# Revit family: lgh-n15_35rkx2(d)_rks2(d)_60Hz
name_source: partatom
category: 機械設備
units: mm (PartAtom-declared; Revit-internal decimal feet)

## family parameters
OmniClass タイトル = Heat Exchangers for Ventilation Air
OmniClass 番号 = 23.75.10.34.21
パーツ タイプ = 標準
ロード時にボイドで切り取り = いいえ
丸型コネクタ寸法 = 直径を使用
作業面ベース = いいえ
共有 = いいえ
常に垂直 = はい
部屋計算ポイント = はい

## types (12) — shared parameters
Box_Depth = 172  [stored 0.564304 ft]
Box_Height = 262  [stored 0.85958 ft]
Box_Width = 115  [stored 0.377297 ft]
Clearance Left = 600
EAダクト接続口方向_変更 = いいえ
EAダクト接続口方向_標準 = はい
IfcExportAs = IfcAirToAirHeatRecoveryType
IfcExportType = ROTARYWHEEL
OAダクト接続口方向_変更 = いいえ
OAダクト接続口方向_標準 = はい
OmniClassCode = 23-27 23 19 11
URL = https://www.mitsubishielectric.co.jp
Uniclass2015Code = Pr_60_60_36_88
Uniclass2015Title = Thermal wheels
Uniclass2015Version = Systems v1.9
ドレン管_D = 307  [stored 1.00722 ft]
ドレン管_Depth = 10  [stored 0.0328084 ft]
ドレン管_H = 25  [stored 0.082021 ft]
ドレン管径 = 32 mm
メンテナンススペース = はい
仕様書バージョン = Version1.0
企業コード = 108420
分類コード = 50052504100070
初期抵抗 = 0.0 Pa
加湿給水管径 = 22 mm
周波数 = 60 Hz
呼称 = 全熱交換ユニット
外気量 = 0.0 m³/h
天吊金具_幅 = 20  [stored 0.0656168 ft]
天吊金具_径 = 7  [stored 0.0229659 ft]
実風量 = 0.0 m³/h
形式 = 天井埋込ダクト形
排気量 = 0.0 m³/h
本体マテリアル = 溶融亜鉛めっき鋼板
法定耐用年数 = 15
消費電力_加湿器 = 0 W
点検口 = はい
点検口1_Depth = 450  [stored 1.47638 ft]
点検口1_Width = 450  [stored 1.47638 ft]
点検口離隔 = 150
相 = 1
積算_科目 = 1 空気調和設備
符号 = HEU
給水管_D = 358  [stored 1.17454 ft]
給水管_Depth = 10  [stored 0.0328084 ft]
給水管_H = 92  [stored 0.301837 ft]
製品リリース年月 = 2015/1/30
製品出荷対象 = 国内
製造元 = 三菱電機株式会社
設置方法 = 天井吊(隠ぺい)形
設計風量 = 0.0 m³/h
説明 = 業務用ロスナイ 天井埋込形加湿付
負荷分類 = 3_ファン類
運転質量 = 0.00 kg
電動機出力 = 0 W
zero-valued in all types: Clearance Bottom, Clearance Top, EAサイズ_W, OAサイズ_W, RAサイズ_W, SAサイズ_W

## per-type parameters (varying)
- LGH-N15RKS2: Box_D=446  [stored 1.46325 ft]; Box_H=20  [stored 0.0656168 ft]; Depth=1182; Duct_Change_Center=119  [stored 0.39042 ft]; Duct_Depth=53  [stored 0.173885 ft]; Duct_Height=95; Duct_Height_SA=149  [stored 0.488845 ft]; Duct_Pitch_OA_EA=450  [stored 1.47638 ft]; Duct_Pitch_SA_RA=400  [stored 1.31234 ft]; Duct_Width_RA=225  [stored 0.738189 ft]; EAサイズ_D=98; Height=298  [stored 0.97769 ft]; MAX静圧=130.0 Pa; MAX風量=150.0 m³/h; MID静圧=60.0 Pa; MID風量=100.0 m³/h; MIN静圧=15.0 Pa; MIN風量=50.0 m³/h; OAサイズ_D=98; RAサイズ_D=98; SAサイズ_D=98; SMAX静圧=0.0 Pa; SMAX風量=0.0 m³/h; Width=611; エンタルピ交換効率_冷房=68.00%; エンタルピ交換効率_暖房=69.00%; 価格=328000 $; 吊りボルト_高さ=75; 吊りボルトピッチ1=658; 吊りボルトピッチ2=1169; 有効加湿量=0.44; 極数=2; 機外静圧=130.0 Pa; 機外静圧_排気=130.0 Pa; 消費電力=133 W; 温度交換効率=74.00%; 点検口1_Center=656; 点検口高さ=-298  [stored -0.97769 ft]; 製品質量=33.00 kg; 質量=39.60 kg; 電圧=100 V; 面風速=5.3 m/s; 風量=150.0 m³/h; 騒音レベル(dB(A))=29
- LGH-N15RKS2D: Box_D=446  [stored 1.46325 ft]; Box_H=20  [stored 0.0656168 ft]; Depth=1182; Duct_Change_Center=119  [stored 0.39042 ft]; Duct_Depth=53  [stored 0.173885 ft]; Duct_Height=95; Duct_Height_SA=149  [stored 0.488845 ft]; Duct_Pitch_OA_EA=450  [stored 1.47638 ft]; Duct_Pitch_SA_RA=400  [stored 1.31234 ft]; Duct_Width_RA=225  [stored 0.738189 ft]; EAサイズ_D=98; Height=298  [stored 0.97769 ft]; MAX静圧=130.0 Pa; MAX風量=150.0 m³/h; MID静圧=60.0 Pa; MID風量=100.0 m³/h; MIN静圧=21.0 Pa; MIN風量=60.0 m³/h; OAサイズ_D=98; RAサイズ_D=98; SAサイズ_D=98; SMAX静圧=0.0 Pa; SMAX風量=0.0 m³/h; Width=611; エンタルピ交換効率_冷房=68.00%; エンタルピ交換効率_暖房=69.00%; 価格=328000 $; 吊りボルト_高さ=75; 吊りボルトピッチ1=658; 吊りボルトピッチ2=1169; 有効加湿量=0.44; 極数=3; 機外静圧=130.0 Pa; 機外静圧_排気=130.0 Pa; 消費電力=125 W; 温度交換効率=74.00%; 点検口1_Center=656; 点検口高さ=-298  [stored -0.97769 ft]; 製品質量=33.00 kg; 質量=39.60 kg; 電圧=200 V; 面風速=5.3 m/s; 風量=150.0 m³/h; 騒音レベル(dB(A))=29
- LGH-N15RKX2: Box_D=446  [stored 1.46325 ft]; Box_H=20  [stored 0.0656168 ft]; Depth=1182; Duct_Change_Center=119  [stored 0.39042 ft]; Duct_Depth=53  [stored 0.173885 ft]; Duct_Height=95; Duct_Height_SA=149  [stored 0.488845 ft]; Duct_Pitch_OA_EA=450  [stored 1.47638 ft]; Duct_Pitch_SA_RA=400  [stored 1.31234 ft]; Duct_Width_RA=225  [stored 0.738189 ft]; EAサイズ_D=98; Height=298  [stored 0.97769 ft]; MAX静圧=130.0 Pa; MAX風量=150.0 m³/h; MID静圧=60.0 Pa; MID風量=100.0 m³/h; MIN静圧=15.0 Pa; MIN風量=50.0 m³/h; OAサイズ_D=98; RAサイズ_D=98; SAサイズ_D=98; SMAX静圧=0.0 Pa; SMAX風量=0.0 m³/h; Width=611; エンタルピ交換効率_冷房=68.00%; エンタルピ交換効率_暖房=69.00%; 価格=475000 $; 参照している仕様書等のバージョン=公共建築工事標準仕様書（機械設備工事編）平成31年度版; 吊りボルト_高さ=75; 吊りボルトピッチ1=658; 吊りボルトピッチ2=1169; 有効加湿量=0.44; 極数=2; 機外静圧=130.0 Pa; 機外静圧_排気=130.0 Pa; 消費電力=133 W; 温度交換効率=74.00%; 点検口1_Center=656; 点検口高さ=-298  [stored -0.97769 ft]; 製品質量=33.00 kg; 質量=39.60 kg; 電圧=100 V; 面風速=5.3 m/s; 風量=150.0 m³/h; 騒音レベル(dB(A))=29
- LGH-N15RKX2D: Box_D=446  [stored 1.46325 ft]; Box_H=20  [stored 0.0656168 ft]; Depth=1182; Duct_Change_Center=119  [stored 0.39042 ft]; Duct_Depth=53  [stored 0.173885 ft]; Duct_Height=95; Duct_Height_SA=149  [stored 0.488845 ft]; Duct_Pitch_OA_EA=450  [stored 1.47638 ft]; Duct_Pitch_SA_RA=400  [stored 1.31234 ft]; Duct_Width_RA=225  [stored 0.738189 ft]; EAサイズ_D=98; Height=298  [stored 0.97769 ft]; MAX静圧=130.0 Pa; MAX風量=150.0 m³/h; MID静圧=60.0 Pa; MID風量=100.0 m³/h; MIN静圧=21.0 Pa; MIN風量=60.0 m³/h; OAサイズ_D=98; RAサイズ_D=98; SAサイズ_D=98; SMAX静圧=0.0 Pa; SMAX風量=0.0 m³/h; Width=611; エンタルピ交換効率_冷房=68.00%; エンタルピ交換効率_暖房=69.00%; 価格=475000 $; 参照している仕様書等のバージョン=公共建築工事標準仕様書（機械設備工事編）平成31年度版; 吊りボルト_高さ=75; 吊りボルトピッチ1=658; 吊りボルトピッチ2=1169; 有効加湿量=0.44; 極数=3; 機外静圧=130.0 Pa; 機外静圧_排気=130.0 Pa; 消費電力=125 W; 温度交換効率=74.00%; 点検口1_Center=656; 点検口高さ=-298  [stored -0.97769 ft]; 製品質量=33.00 kg; 質量=39.60 kg; 電圧=200 V; 面風速=5.3 m/s; 風量=150.0 m³/h; 騒音レベル(dB(A))=29
- LGH-N25RKS2: Box_D=476  [stored 1.56168 ft]; Box_H=20  [stored 0.0656168 ft]; Depth=1212; Duct_Change_Center=102; Duct_Depth=63  [stored 0.206693 ft]; Duct_Height=115  [stored 0.377297 ft]; Duct_Height_SA=149  [stored 0.488845 ft]; Duct_Pitch_OA_EA=530  [stored 1.73885 ft]; Duct_Pitch_SA_RA=505  [stored 1.65682 ft]; Duct_Width_RA=265  [stored 0.869423 ft]; EAサイズ_D=142  [stored 0.465879 ft]; Height=298  [stored 0.97769 ft]; MAX静圧=90.0 Pa; MAX風量=250.0 m³/h; MID静圧=30.0 Pa; MID風量=145.0 m³/h; MIN静圧=7.0 Pa; MIN風量=70.0 m³/h; OAサイズ_D=142  [stored 0.465879 ft]; RAサイズ_D=142  [stored 0.465879 ft]; SAサイズ_D=142  [stored 0.465879 ft]; SMAX静圧=0.0 Pa; SMAX風量=0.0 m³/h; Width=735; エンタルピ交換効率_冷房=68.00%; エンタルピ交換効率_暖房=69.00%; 価格=356000 $; 吊りボルト_高さ=75; 吊りボルトピッチ1=782; 吊りボルトピッチ2=1199; 有効加湿量=0.73; 極数=2; 機外静圧=90.0 Pa; 機外静圧_排気=90.0 Pa; 消費電力=162 W; 温度交換効率=74.00%; 点検口1_Center=656; 点検口高さ=-298  [stored -0.97769 ft]; 製品質量=36.00 kg; 質量=43.20 kg; 電圧=100 V; 面風速=3.9 m/s; 風量=250.0 m³/h; 騒音レベル(dB(A))=29
- LGH-N25RKS2D: Box_D=476  [stored 1.56168 ft]; Box_H=20  [stored 0.0656168 ft]; Depth=1212; Duct_Change_Center=102; Duct_Depth=63  [stored 0.206693 ft]; Duct_Height=115  [stored 0.377297 ft]; Duct_Height_SA=149  [stored 0.488845 ft]; Duct_Pitch_OA_EA=530  [stored 1.73885 ft]; Duct_Pitch_SA_RA=505  [stored 1.65682 ft]; Duct_Width_RA=265  [stored 0.869423 ft]; EAサイズ_D=142  [stored 0.465879 ft]; Height=298  [stored 0.97769 ft]; MAX静圧=90.0 Pa; MAX風量=250.0 m³/h; MID静圧=35.0 Pa; MID風量=155.0 m³/h; MIN静圧=7.0 Pa; MIN風量=70.0 m³/h; OAサイズ_D=142  [stored 0.465879 ft]; RAサイズ_D=142  [stored 0.465879 ft]; SAサイズ_D=142  [stored 0.465879 ft]; SMAX静圧=0.0 Pa; SMAX風量=0.0 m³/h; Width=735; エンタルピ交換効率_冷房=68.00%; エンタルピ交換効率_暖房=69.00%; 価格=356000 $; 吊りボルト_高さ=75; 吊りボルトピッチ1=782; 吊りボルトピッチ2=1199; 有効加湿量=0.73; 極数=3; 機外静圧=90.0 Pa; 機外静圧_排気=90.0 Pa; 消費電力=173 W; 温度交換効率=74.00%; 点検口1_Center=656; 点検口高さ=-298  [stored -0.97769 ft]; 製品質量=36.00 kg; 質量=43.20 kg; 電圧=200 V; 面風速=3.9 m/s; 風量=250.0 m³/h; 騒音レベル(dB(A))=29
- LGH-N25RKX2: Box_D=476  [stored 1.56168 ft]; Box_H=20  [stored 0.0656168 ft]; Depth=1212; Duct_Change_Center=102; Duct_Depth=63  [stored 0.206693 ft]; Duct_Height=115  [stored 0.377297 ft]; Duct_Height_SA=149  [stored 0.488845 ft]; Duct_Pitch_OA_EA=530  [stored 1.73885 ft]; Duct_Pitch_SA_RA=505  [stored 1.65682 ft]; Duct_Width_RA=265  [stored 0.869423 ft]; EAサイズ_D=142  [stored 0.465879 ft]; Height=298  [stored 0.97769 ft]; MAX静圧=90.0 Pa; MAX風量=250.0 m³/h; MID静圧=30.0 Pa; MID風量=145.0 m³/h; MIN静圧=7.0 Pa; MIN風量=70.0 m³/h; OAサイズ_D=142  [stored 0.465879 ft]; RAサイズ_D=142  [stored 0.465879 ft]; SAサイズ_D=142  [stored 0.465879 ft]; SMAX静圧=0.0 Pa; SMAX風量=0.0 m³/h; Width=735; エンタルピ交換効率_冷房=68.00%; エンタルピ交換効率_暖房=69.00%; 価格=515000 $; 参照している仕様書等のバージョン=公共建築工事標準仕様書（機械設備工事編）平成31年度版; 吊りボルト_高さ=75; 吊りボルトピッチ1=782; 吊りボルトピッチ2=1199; 有効加湿量=0.73; 極数=2; 機外静圧=90.0 Pa; 機外静圧_排気=90.0 Pa; 消費電力=162 W; 温度交換効率=74.00%; 点検口1_Center=656; 点検口高さ=-298  [stored -0.97769 ft]; 製品質量=36.00 kg; 質量=43.20 kg; 電圧=100 V; 面風速=3.9 m/s; 風量=250.0 m³/h; 騒音レベル(dB(A))=29
- LGH-N25RKX2D: Box_D=476  [stored 1.56168 ft]; Box_H=20  [stored 0.0656168 ft]; Depth=1212; Duct_Change_Center=102; Duct_Depth=63  [stored 0.206693 ft]; Duct_Height=115  [stored 0.377297 ft]; Duct_Height_SA=149  [stored 0.488845 ft]; Duct_Pitch_OA_EA=530  [stored 1.73885 ft]; Duct_Pitch_SA_RA=505  [stored 1.65682 ft]; Duct_Width_RA=265  [stored 0.869423 ft]; EAサイズ_D=142  [stored 0.465879 ft]; Height=298  [stored 0.97769 ft]; MAX静圧=90.0 Pa; MAX風量=250.0 m³/h; MID静圧=35.0 Pa; MID風量=155.0 m³/h; MIN静圧=7.0 Pa; MIN風量=70.0 m³/h; OAサイズ_D=142  [stored 0.465879 ft]; RAサイズ_D=142  [stored 0.465879 ft]; SAサイズ_D=142  [stored 0.465879 ft]; SMAX静圧=0.0 Pa; SMAX風量=0.0 m³/h; Width=735; エンタルピ交換効率_冷房=68.00%; エンタルピ交換効率_暖房=69.00%; 価格=515000 $; 参照している仕様書等のバージョン=公共建築工事標準仕様書（機械設備工事編）平成31年度版; 吊りボルト_高さ=75; 吊りボルトピッチ1=782; 吊りボルトピッチ2=1199; 有効加湿量=0.73; 極数=3; 機外静圧=90.0 Pa; 機外静圧_排気=90.0 Pa; 消費電力=173 W; 温度交換効率=74.00%; 点検口1_Center=656; 点検口高さ=-298  [stored -0.97769 ft]; 製品質量=36.00 kg; 質量=43.20 kg; 電圧=200 V; 面風速=3.9 m/s; 風量=250.0 m³/h; 騒音レベル(dB(A))=29
- LGH-N35RKS2: Box_D=476  [stored 1.56168 ft]; Box_H=12  [stored 0.0393701 ft]; Depth=1288; Duct_Change_Center=124  [stored 0.406824 ft]; Duct_Depth=64  [stored 0.209974 ft]; Duct_Height=110  [stored 0.360892 ft]; Duct_Height_SA=165; Duct_Pitch_OA_EA=650; Duct_Pitch_SA_RA=400  [stored 1.31234 ft]; Duct_Width_RA=325  [stored 1.06627 ft]; EAサイズ_D=142  [stored 0.465879 ft]; Height=331  [stored 1.08596 ft]; MAX静圧=85.0 Pa; MAX風量=350.0 m³/h; MID静圧=50.0 Pa; MID風量=250.0 m³/h; MIN静圧=7.0 Pa; MIN風量=110.0 m³/h; OAサイズ_D=142  [stored 0.465879 ft]; RAサイズ_D=142  [stored 0.465879 ft]; SAサイズ_D=142  [stored 0.465879 ft]; SMAX静圧=170.0 Pa; SMAX風量=350.0 m³/h; Width=874; エンタルピ交換効率_冷房=70.00%; エンタルピ交換効率_暖房=71.00%; 価格=406000 $; 吊りボルト_高さ=85  [stored 0.278871 ft]; 吊りボルトピッチ1=922; 吊りボルトピッチ2=1275; 有効加湿量=1.01; 極数=2; 機外静圧=170.0 Pa; 機外静圧_排気=170.0 Pa; 消費電力=227 W; 温度交換効率=75.00%; 点検口1_Center=732; 点検口高さ=-331  [stored -1.08596 ft]; 製品質量=44.00 kg; 質量=52.80 kg; 電圧=100 V; 面風速=5.5 m/s; 風量=350.0 m³/h; 騒音レベル(dB(A))=32.5
- LGH-N35RKS2D: Box_D=476  [stored 1.56168 ft]; Box_H=12  [stored 0.0393701 ft]; Depth=1288; Duct_Change_Center=124  [stored 0.406824 ft]; Duct_Depth=64  [stored 0.209974 ft]; Duct_Height=110  [stored 0.360892 ft]; Duct_Height_SA=165; Duct_Pitch_OA_EA=650; Duct_Pitch_SA_RA=400  [stored 1.31234 ft]; Duct_Width_RA=325  [stored 1.06627 ft]; EAサイズ_D=142  [stored 0.465879 ft]; Height=331  [stored 1.08596 ft]; MAX静圧=85.0 Pa; MAX風量=350.0 m³/h; MID静圧=40.0 Pa; MID風量=245.0 m³/h; MIN静圧=10.0 Pa; MIN風量=135.0 m³/h; OAサイズ_D=142  [stored 0.465879 ft]; RAサイズ_D=142  [stored 0.465879 ft]; SAサイズ_D=142  [stored 0.465879 ft]; SMAX静圧=170.0 Pa; SMAX風量=350.0 m³/h; Width=874; エンタルピ交換効率_冷房=70.00%; エンタルピ交換効率_暖房=71.00%; 価格=406000 $; 吊りボルト_高さ=85  [stored 0.278871 ft]; 吊りボルトピッチ1=922; 吊りボルトピッチ2=1275; 有効加湿量=1.01; 極数=3; 機外静圧=170.0 Pa; 機外静圧_排気=170.0 Pa; 消費電力=212 W; 温度交換効率=75.00%; 点検口1_Center=732; 点検口高さ=-331  [stored -1.08596 ft]; 製品質量=44.00 kg; 質量=52.80 kg; 電圧=200 V; 面風速=5.5 m/s; 風量=350.0 m³/h; 騒音レベル(dB(A))=32.5
- LGH-N35RKX2: Box_D=476  [stored 1.56168 ft]; Box_H=12  [stored 0.0393701 ft]; Depth=1288; Duct_Change_Center=124  [stored 0.406824 ft]; Duct_Depth=64  [stored 0.209974 ft]; Duct_Height=110  [stored 0.360892 ft]; Duct_Height_SA=165; Duct_Pitch_OA_EA=650; Duct_Pitch_SA_RA=400  [stored 1.31234 ft]; Duct_Width_RA=325  [stored 1.06627 ft]; EAサイズ_D=142  [stored 0.465879 ft]; Height=331  [stored 1.08596 ft]; MAX静圧=85.0 Pa; MAX風量=350.0 m³/h; MID静圧=50.0 Pa; MID風量=250.0 m³/h; MIN静圧=7.0 Pa; MIN風量=110.0 m³/h; OAサイズ_D=142  [stored 0.465879 ft]; RAサイズ_D=142  [stored 0.465879 ft]; SAサイズ_D=142  [stored 0.465879 ft]; SMAX静圧=170.0 Pa; SMAX風量=350.0 m³/h; Width=874; エンタルピ交換効率_冷房=70.00%; エンタルピ交換効率_暖房=71.00%; 価格=573000 $; 参照している仕様書等のバージョン=公共建築工事標準仕様書（機械設備工事編）平成31年度版; 吊りボルト_高さ=85  [stored 0.278871 ft]; 吊りボルトピッチ1=922; 吊りボルトピッチ2=1275; 有効加湿量=1.01; 極数=2; 機外静圧=170.0 Pa; 機外静圧_排気=170.0 Pa; 消費電力=227 W; 温度交換効率=75.00%; 点検口1_Center=732; 点検口高さ=-331  [stored -1.08596 ft]; 製品質量=44.00 kg; 質量=52.80 kg; 電圧=100 V; 面風速=5.5 m/s; 風量=350.0 m³/h; 騒音レベル(dB(A))=32.5
- LGH-N35RKX2D: Box_D=476  [stored 1.56168 ft]; Box_H=12  [stored 0.0393701 ft]; Depth=1288; Duct_Change_Center=124  [stored 0.406824 ft]; Duct_Depth=64  [stored 0.209974 ft]; Duct_Height=110  [stored 0.360892 ft]; Duct_Height_SA=165; Duct_Pitch_OA_EA=650; Duct_Pitch_SA_RA=400  [stored 1.31234 ft]; Duct_Width_RA=325  [stored 1.06627 ft]; EAサイズ_D=142  [stored 0.465879 ft]; Height=331  [stored 1.08596 ft]; MAX静圧=85.0 Pa; MAX風量=350.0 m³/h; MID静圧=40.0 Pa; MID風量=245.0 m³/h; MIN静圧=10.0 Pa; MIN風量=135.0 m³/h; OAサイズ_D=142  [stored 0.465879 ft]; RAサイズ_D=142  [stored 0.465879 ft]; SAサイズ_D=142  [stored 0.465879 ft]; SMAX静圧=170.0 Pa; SMAX風量=350.0 m³/h; Width=874; エンタルピ交換効率_冷房=70.00%; エンタルピ交換効率_暖房=71.00%; 価格=573000 $; 参照している仕様書等のバージョン=公共建築工事標準仕様書（機械設備工事編）平成31年度版; 吊りボルト_高さ=85  [stored 0.278871 ft]; 吊りボルトピッチ1=922; 吊りボルトピッチ2=1275; 有効加湿量=1.01; 極数=3; 機外静圧=170.0 Pa; 機外静圧_排気=170.0 Pa; 消費電力=212 W; 温度交換効率=75.00%; 点検口1_Center=732; 点検口高さ=-331  [stored -1.08596 ft]; 製品質量=44.00 kg; 質量=52.80 kg; 電圧=200 V; 面風速=5.5 m/s; 風量=350.0 m³/h; 騒音レベル(dB(A))=32.5

note: column(s) folded — value = type name in every type: モデル

note: [stored X ft] marks values corroborated as IEEE doubles in the binary element streams (Revit-internal decimal feet)

## geometry (parser evidence)
native form markers: Blend x4
no freeform markers — native parametric forms only
